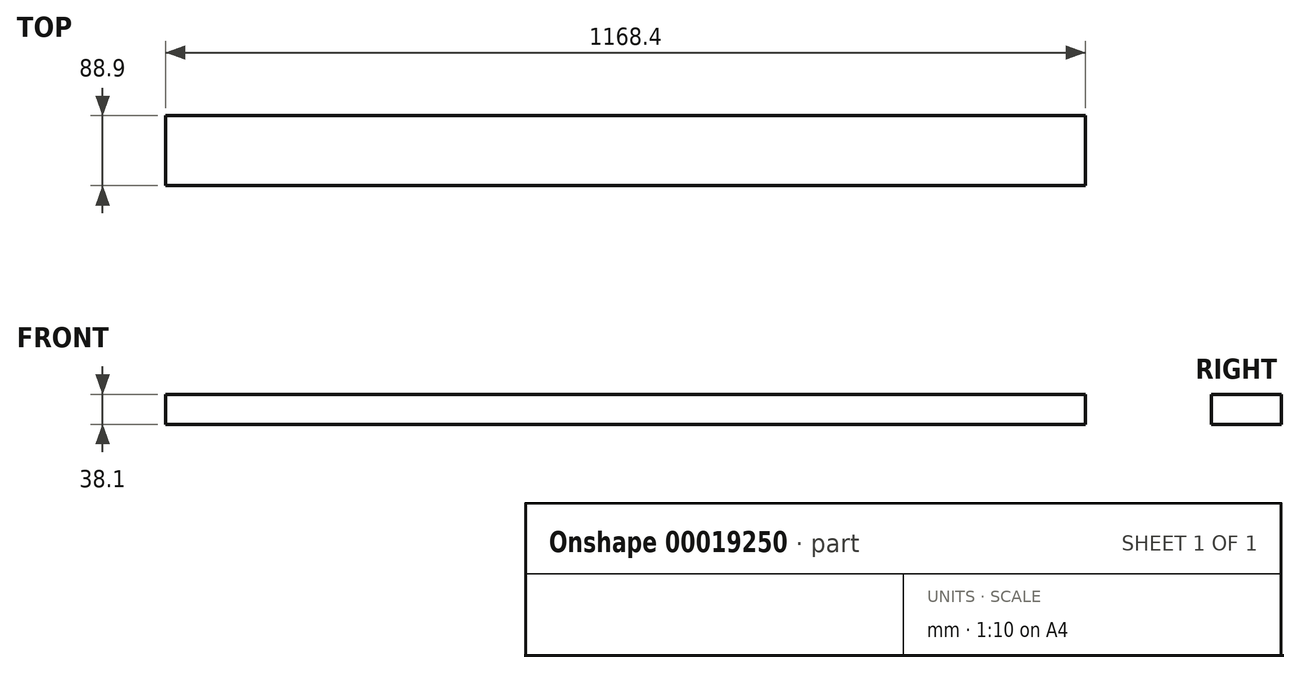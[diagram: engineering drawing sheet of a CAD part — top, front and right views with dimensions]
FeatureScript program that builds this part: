
annotation { "Feature Type Name" : "Feature", "Feature Type Description" : "" }
export const myFeature = defineFeature(function(context is Context, id is Id, definition is map)
    precondition{}
    {
        {
            var Q0;
            Q0=qCreatedBy(makeId("Top.planeOp"),FACE);
            var sketch = newSketch(context, id + "F0", { "sketchPlane" : qUnion([Q0])});
            skLineSegment(sketch, "E0.bottom", {"start": v(0, 0) * mm, "end": v(1168.4, 0) * mm});
            skLineSegment(sketch, "E0.top", {"start": v(0, -88.9) * mm, "end": v(1168.4, -88.9) * mm});
            skLineSegment(sketch, "E0.left", {"start": v(0, 0) * mm, "end": v(0, -88.9) * mm});
            skLineSegment(sketch, "E0.right", {"start": v(1168.4, 0) * mm, "end": v(1168.4, -88.9) * mm});
            skSolve(sketch);
        }
        {
            var Q0;
            Q0 = qSketchRegion(id + "F0", true);
            extrude(context, id + "F1", {"entities" : qUnion([Q0]), "depth" : 38.1 * mm});
        }
    });
